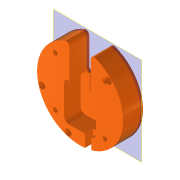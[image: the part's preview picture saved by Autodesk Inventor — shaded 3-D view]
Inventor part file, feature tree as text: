
AUTODESK INVENTOR PART (.ipt)
format: ipt  version: 2022 (Build 260153000, 153)  size: 357,888 bytes
history: native  units: mm
features: reference x56, other x14, extrude x7, sketch x6, projected_geometry x4, plane x3, hole x2, fillet x2, chamfer x1
ambient origin geometry x8: Origin, YZ Plane, XZ Plane, XY Plane, X Axis, Y Axis, Z Axis, Center Point
bodies: Solid1 (feature_tree)
feature tree (95):
  plane  "Work Plane1"
  extrude  "Extrusion1"  Depth=7.5mm
  extrude  "Extrusion26"  Depth=10.0mm TaperAngle=45.0deg
  chamfer  "Fase2"  [1 undecoded]
  plane  "Arbeitsebene9"
  extrude  "Extrusion29"  Depth=5.0mm
  extrude  "Extrusion30"  Depth=5.0mm
  plane  "Arbeitsebene10"
  hole  "Bohrung2"  [1 undecoded]
  extrude  "Extrusion32"  Depth=5.0mm TaperAngle=0.0deg
  extrude  "Extrusion33"  TaperAngle=0.0deg  [1 undecoded]
  fillet  "Rundung4"  Radius=2.0mm
  fillet  "Rundung5"  Radius=52.0mm
  hole  "Bohrung3"  [1 undecoded]
  extrude  "Extrusion34"  Depth=5.0mm TaperAngle=0.0deg
  reference  "Reference1"
  reference  "Reference2"
  reference  "Reference3"
  reference  "Reference4"
  reference  "Reference9"
  reference  "Reference20"
  reference  "Reference21"
  reference  "Reference22"
  reference  "Reference23"
  reference  "Reference24"
  sketch  "Skizze31"  dims[d10=12.0mm d11=0.0mm d181=7.5mm]
  projected_geometry  "Projizierte Kontur17"
  sketch  "Skizze34"  dims[d182=10.0mm d183=0.0mm d184=0.5mm d185=2.0mm d186=45.0deg]
  reference  "Referenz35"
  sketch  "Skizze35"  dims[d193=-1.5mm]
  reference  "Referenz36"
  sketch  "Skizze37"  dims[d194=8.6mm]
  projected_geometry  "Projizierte Kontur18"
  reference  "Referenz41"
  sketch  "Skizze38"  dims[d195=8.6mm d196=0.0mm d197=0.0mm]
  projected_geometry  "Projizierte Kontur19"
  reference  "Referenz42"
  sketch  "Skizze40"  dims[d198=10.0mm d199=0.0mm d204=30.0mm d205=30.0mm d206=2.8mm d207=6.0mm d208=8.0mm d209=6.0mm d210=90.0deg d211=8.0mm d212=20.594885mm d213=4.0mm d214=5.0mm d215=0.0mm d216=0.0mm d217=0.0mm d218=2.0mm d219=52.0mm d220=2.0mm d221=4.0mm d222=6.0mm d223=4.0mm d224=2.0mm d225=90.0deg d226=8.0mm d227=20.594885mm d228=5.0mm d229=0.0mm d230=11.58mm d231=11.58mm d232=2.6mm d233=2.6mm d160=0.5mm d161=0.872665mm d162=0.5mm d163=0.872665mm]
  reference  "Referenz43"
  reference  "Referenz44"
  reference  "Referenz45"
  reference  "Referenz46"
  reference  "Referenz47"
  projected_geometry  "Projizierte Kontur20"
  reference  "Referenz48"
  reference  "Referenz49"
  reference  "Referenz50"
  reference  "Referenz51"
  reference  "Referenz52"
  reference  "Referenz53"
  reference  "Referenz54"
  reference  "Referenz55"
  reference  "Referenz56"
  reference  "Referenz57"
  reference  "Referenz58"
  reference  "Referenz59"
  reference  "Referenz60"
  reference  "Referenz61"
  reference  "Referenz62"
  reference  "Referenz63"
  reference  "Referenz64"
  reference  "Referenz65"
  reference  "Referenz66"
  reference  "Referenz67"
  reference  "Referenz68"
  reference  "Referenz69"
  reference  "Referenz70"
  reference  "Referenz71"
  reference  "Referenz72"
  reference  "Referenz73"
  reference  "Referenz74"
  reference  "Referenz75"
  reference  "Referenz76"
  reference  "Referenz77"
  reference  "Referenz78"
  reference  "Referenz79"
  reference  "Referenz80"
  reference  "Referenz81"
  reference  "Referenz82"
  reference  "Referenz83"
  reference  "Referenz84"
  other  "Assembly_Cube_v2_Thorlabs.iam"
  other  "10_Cube_Base:1"
  other  "00_Base_v0:1"
  other  "Assembly_Cube_Kinematic_Mirrormount_v2.iam"
  other  "Assembly_Cube_empty_1x1_v2:1"
  other  "10_Cube_1x1_v2:1"
  other  "10_Lid_1x1_v2:1"
  other  "Assembly_Cube_SEEED_Xiao_Sense_Camera_v3.iam"
  other  "00_Seeeduino Xiao:1"
  other  "Assembly_Matchboxscope_injectionmolded.iam"
  other  "IM_Matchboxscope_base_old:2"
  other  "IM_Matchboxscope_base_old:3"
  other  "IM_Matchboxscope_plate:4"
  other  "10_Cube_Lid:1"
note: 4 required parameter values undecoded (feature->parameter linkage not recoverable at this tier; creation-order binding heuristic only, values carry confidence <= 0.55)
